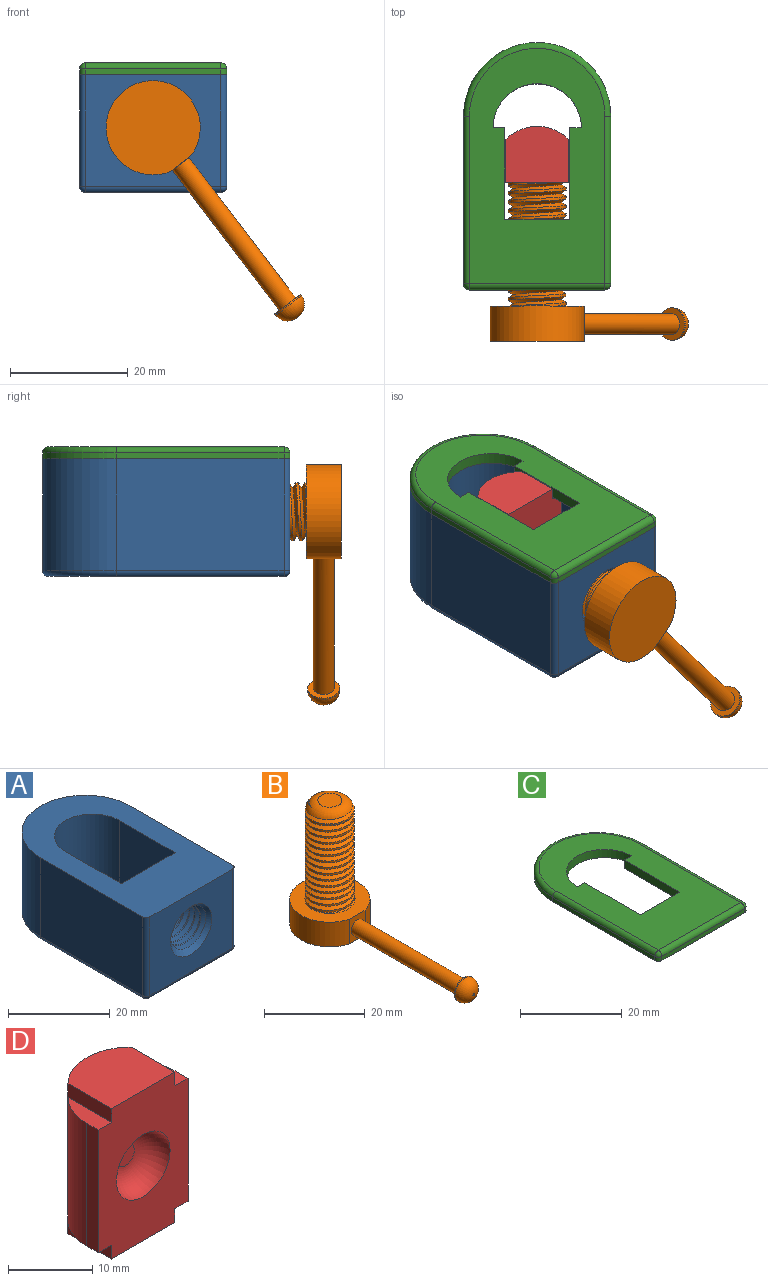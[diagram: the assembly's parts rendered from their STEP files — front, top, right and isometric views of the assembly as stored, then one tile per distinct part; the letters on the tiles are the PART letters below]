
ASSEMBLY  parts=4 mates=3
PART A: 30 faces, bbox 27.1x43.3x20 mm
  f0: cylinder r=4.25mm len=9mm, axis (0,-1,0), area 55mm2, adj f17,f18,f19,f20,f21
  f1: plane 15.5x2mm, normal (0,0,1), area 31mm2, adj f5,f9,f10,f15
  f2: plane 28.5x19mm, normal (-1,0,0), area 541.5mm2, adj f11,f16,f22,f24
  f3: plane 23x19mm, normal (0,-1,0), area 333.1mm2, adj f16,f17,f22,f25,f26
  f4: plane 28.5x19mm, normal (1,0,0), area 541.5mm2, adj f11,f16,f26,f29
  f5: plane 2x2mm, normal (0,1,0), area 4mm2, adj f1,f6,f10,f13
  f6: cylinder r=7.5mm len=20mm, axis (0,0,-1), area 471.2mm2, adj f5,f7,f13,f14,f15,f16
  f7: plane 2x2mm, normal (0,1,0), area 4mm2, adj f6,f8,f12,f13
  f8: plane 15.5x2mm, normal (-1,0,0), area 31mm2, adj f7,f9,f12,f13
  f9: plane 20x15mm, normal (0,1,0), area 188.1mm2, adj f1,f8,f10,f12,f13,f14,f15,f16
  f10: plane 15.5x2mm, normal (1,0,0), area 31mm2, adj f1,f5,f9,f13
  f11: cylinder r=12.5mm len=25mm, axis (0,0,-1), area 746.1mm2, adj f2,f4,f16,f27
  f12: plane 15.5x2mm, normal (0,0,1), area 31mm2, adj f7,f8,f9,f14
  f13: plane 40x23mm, normal (0,0,-1), area 604.4mm2, adj f5,f6,f7,f8,f9,f10,f24,f25
  f14: plane 18x15.5mm, normal (-1,0,0), area 279mm2, adj f6,f9,f12,f16
  f15: plane 18x15.5mm, normal (1,0,0), area 279mm2, adj f1,f6,f9,f16
  f16: plane 42x25mm, normal (0,0,1), area 661.7mm2, adj f2,f3,f4,f6,f9,f11,f14,f15
  f17: cone r=4.25mm half-angle=45deg, axis (0,-1,0), area 50.7mm2, adj f0,f3,f20,f21
  f18: cone r=4.25mm half-angle=45deg, axis (0,1,0), area 50.4mm2, adj f0,f9,f19,f20,f21
  f19: cone r=4.25mm half-angle=45deg, axis (0,1,0), area 0.2mm2, adj f0,f18,f21
  f20: bspline ~12.14x11.9mm, area 232.8mm2, adj f0,f17,f18,f21
  f21: bspline ~12.14x11.9mm, area 233mm2, adj f0,f17,f18,f19,f20
  f22: cylinder r=1mm len=19mm, axis (0,0,-1), area 29.8mm2, adj f2,f3,f16,f23
  f23: sphere r=1mm, area 1.6mm2, adj f22,f24,f25
  f24: cylinder r=1mm len=28.5mm, axis (0,-1,0), area 44.8mm2, adj f2,f13,f23,f27
  f25: cylinder r=1mm len=23mm, axis (1,0,0), area 36.1mm2, adj f3,f13,f23,f28
  f26: cylinder r=1mm len=19mm, axis (0,0,1), area 29.8mm2, adj f3,f4,f16,f28
  f27: torus R=11.5mm, axis (0,0,1), area 59.9mm2, adj f11,f13,f24,f29
  f28: sphere r=1mm, area 1.6mm2, adj f25,f26,f29
  f29: cylinder r=1mm len=28.5mm, axis (0,1,0), area 44.8mm2, adj f4,f13,f27,f28
PART B: 17 faces, bbox 16x48.5x30.1 mm
  f0: cylinder r=8mm len=16mm, axis (0,0,-1), area 275mm2, adj f1,f2,f3
  f1: plane 6x4.38mm, normal (0,-1,0), area 16.7mm2, adj f0,f2,f3,f6
  f2: plane 16.02x15.71mm, normal (0,0,1), area 122.5mm2, adj f0,f1,f4,f14,f15,f16
  f3: plane 16x15.69mm, normal (0,0,-1), area 200.2mm2, adj f0,f1
  f4: cylinder r=4.9mm len=21.5mm, axis (0,0,-1), area 187.5mm2, adj f2,f12,f14,f16
  f5: plane 4.8x4.8mm, normal (0,0,1), area 18.1mm2, adj f11
  f6: cylinder r=1.75mm len=30mm, axis (0,1,0), area 329.9mm2, adj f1,f9
  f7: cylinder r=2.75mm len=5.5mm, axis (0,1,0), area 4.3mm2, adj f9,f10
  f8: plane 0.5x0.5mm, normal (0,-1,0), area 0.2mm2, adj f10
  f9: plane 5.5x5.5mm, normal (0,1,0), area 14.1mm2, adj f6,f7
  f10: torus R=0.25mm, axis (0,-1,0), area 45.4mm2, adj f7,f8
  f11: torus R=2.4mm, axis (0,0,1), area 63.6mm2, adj f5,f12,f14,f16
  f12: torus R=2.4mm, axis (0,0,1), area 5.6mm2, adj f4,f11,f14,f16
  f13: plane 1.15x1mm, normal (0,1,0), area 0.6mm2, adj f14,f15,f16
  f14: bspline ~25.33x11.55mm, area 473.6mm2, adj f2,f4,f11,f12,f13,f15,f16
  f15: cylinder r=5mm len=10mm, axis (0,0,-1), area 30mm2, adj f2,f13,f14,f16
  f16: bspline ~25.33x11.55mm, area 458.3mm2, adj f2,f4,f11,f12,f13,f14,f15
PART C: 20 faces, bbox 27.1x43x2 mm
  f0: plane 28.5x1mm, normal (-1,0,0), area 28.5mm2, adj f9,f11,f16,f19
  f1: plane 23x1mm, normal (0,-1,0), area 23mm2, adj f11,f12,f15,f16
  f2: plane 28.5x1mm, normal (1,0,0), area 28.5mm2, adj f9,f11,f12,f14
  f3: plane 2x2mm, normal (0,1,0), area 4mm2, adj f4,f8,f10,f11
  f4: cylinder r=7.5mm len=15mm, axis (0,0,-1), area 47.1mm2, adj f3,f5,f10,f11
  f5: plane 2x2mm, normal (0,1,0), area 4mm2, adj f4,f6,f10,f11
  f6: plane 15.5x2mm, normal (-1,0,0), area 31mm2, adj f5,f7,f10,f11
  f7: plane 11x2mm, normal (0,1,0), area 22mm2, adj f6,f8,f10,f11
  f8: plane 15.5x2mm, normal (1,0,0), area 31mm2, adj f3,f7,f10,f11
  f9: cylinder r=12.5mm len=25mm, axis (0,0,-1), area 39.3mm2, adj f0,f2,f11,f17
  f10: plane 40x23mm, normal (0,0,1), area 604.4mm2, adj f3,f4,f5,f6,f7,f8,f14,f15
  f11: plane 42x25mm, normal (0,0,-1), area 723.7mm2, adj f0,f1,f2,f3,f4,f5,f6,f7
  f12: cylinder r=1mm len=1mm, axis (0,0,1), area 1.6mm2, adj f1,f2,f11,f13
  f13: sphere r=1mm, area 1.6mm2, adj f12,f14,f15
  f14: cylinder r=1mm len=28.5mm, axis (0,-1,0), area 44.8mm2, adj f2,f10,f13,f17
  f15: cylinder r=1mm len=23mm, axis (-1,0,0), area 36.1mm2, adj f1,f10,f13,f18
  f16: cylinder r=1mm len=1mm, axis (0,0,-1), area 1.6mm2, adj f0,f1,f11,f18
  f17: torus R=11.5mm, axis (0,0,1), area 59.9mm2, adj f9,f10,f14,f19
  f18: sphere r=1mm, area 1.6mm2, adj f15,f16,f19
  f19: cylinder r=1mm len=28.5mm, axis (0,1,0), area 44.8mm2, adj f0,f10,f17,f18
PART D: 16 faces, bbox 15x9.5x21.8 mm
  f0: plane 7.31x2.2mm, normal (0,0,-1), area 12.4mm2, adj f2,f4,f5,f13
  f1: plane 7.31x2.2mm, normal (0,0,1), area 12.4mm2, adj f2,f4,f5,f10
  f2: plane 21.8x15mm, normal (0,-1,0), area 245.8mm2, adj f0,f1,f3,f5,f6,f7,f9,f10
  f3: plane 17.8x2mm, normal (1,0,0), area 35.6mm2, adj f2,f4,f6,f7
  f4: cylinder r=7.5mm len=21.8mm, axis (0,0,-1), area 466.5mm2, adj f0,f1,f3,f5,f6,f7,f10,f11
  f5: plane 17.8x2mm, normal (-1,0,0), area 35.6mm2, adj f0,f1,f2,f4
  f6: plane 7.31x2.2mm, normal (0,0,1), area 12.4mm2, adj f2,f3,f4,f11
  f7: plane 7.31x2.2mm, normal (0,0,-1), area 12.4mm2, adj f2,f3,f4,f14
  f8: plane 3x3mm, normal (0,-1,0), area 7.1mm2, adj f9
  f9: torus R=1.5mm, axis (0,-1,0), area 101mm2, adj f2,f8
  f10: plane 7.31x2mm, normal (-1,0,0), area 14.6mm2, adj f1,f2,f4,f12
  f11: plane 7.31x2mm, normal (1,0,0), area 14.6mm2, adj f2,f4,f6,f12
  f12: plane 10.6x9.5mm, normal (0,0,1), area 93.5mm2, adj f2,f4,f10,f11
  f13: plane 7.31x2mm, normal (-1,0,0), area 14.6mm2, adj f0,f2,f4,f15
  f14: plane 7.31x2mm, normal (1,0,0), area 14.6mm2, adj f2,f4,f7,f15
  f15: plane 10.6x9.5mm, normal (0,0,-1), area 93.5mm2, adj f2,f4,f13,f14
PLACE A t=(25.69,26.45,-10.89)mm fixed
PLACE B rot(axis=(-0.23,0.69,0.69),153.9deg) t=(25.99,-1.35,0.11)mm
PLACE C t=(25.69,26.45,9.11)mm
PLACE D t=(36.66,25.65,-8.79)mm
MATE slider A.f0 <-> D.f9  axis (0,1,0) through (25.99,19.39,0.11)mm
MATE fastened A.f16 <-> C.f11  axis (0,0,1) through (25.99,7.39,9.11)mm
MATE revolute D.f9 <-> B.f4  axis (0,-1,0) through (25.99,28.65,0.11)mm
